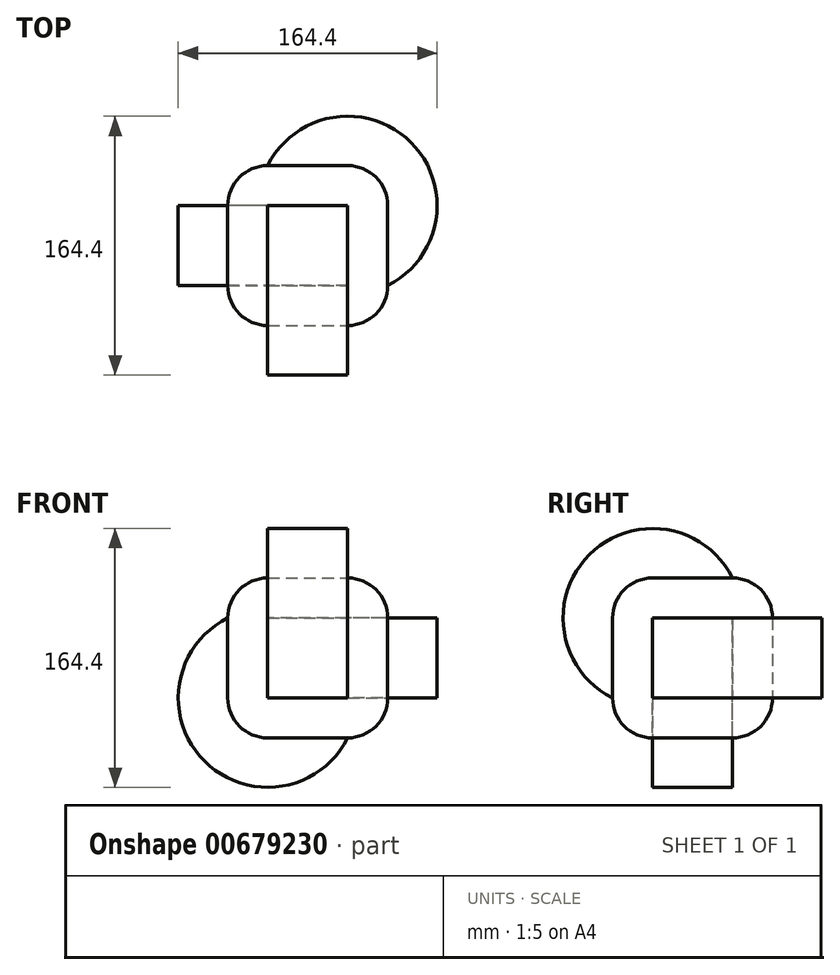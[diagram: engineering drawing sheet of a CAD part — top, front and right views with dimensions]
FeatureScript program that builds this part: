
annotation { "Feature Type Name" : "Feature", "Feature Type Description" : "" }
export const myFeature = defineFeature(function(context is Context, id is Id, definition is map)
    precondition{}
    {
        {
            var Q0;
            Q0=qCreatedBy(makeId("Top.planeOp"),FACE);
            var sketch = newSketch(context, id + "F0", { "sketchPlane" : qUnion([Q0])});
            skLineSegment(sketch, "E0.bottom", {"start": v(-50.8, 50.8) * mm, "end": v(50.8, 50.8) * mm});
            skLineSegment(sketch, "E0.top", {"start": v(-50.8, -50.8) * mm, "end": v(50.8, -50.8) * mm});
            skLineSegment(sketch, "E0.left", {"start": v(-50.8, 50.8) * mm, "end": v(-50.8, -50.8) * mm});
            skLineSegment(sketch, "E0.right", {"start": v(50.8, 50.8) * mm, "end": v(50.8, -50.8) * mm});
            skPoint(sketch, "E0.middle", {"position": v(0, 0) * mm});
            skSolve(sketch);
        }
        {
            var Q0;
            Q0 = qSketchRegion(id + "F0", true);
            extrude(context, id + "F1", {"entities" : qUnion([Q0]), "depth" : 101.6 * mm, "offsetDistance" : 25.4 * mm});
        }
        {
            var Q0;
            Q0=makeQuery(id+"F1.opExtrude","CAP_EDGE",EDGE,{"disambiguationData":[OSD([sQuery(id+"F0.wireOp",EDGE,"E0.right")])],"isStart":false});
            var Q1;
            Q1=makeQuery(id+"F1.opExtrude","CAP_EDGE",EDGE,{"disambiguationData":[OSD([sQuery(id+"F0.wireOp",EDGE,"E0.top")])],"isStart":false});
            var Q2;
            Q2=makeQuery(id+"F1.opExtrude","CAP_EDGE",EDGE,{"disambiguationData":[OSD([sQuery(id+"F0.wireOp",EDGE,"E0.left")])],"isStart":false});
            var Q3;
            Q3=makeQuery(id+"F1.opExtrude","CAP_EDGE",EDGE,{"disambiguationData":[OSD([sQuery(id+"F0.wireOp",EDGE,"E0.bottom")])],"isStart":false});
            var Q4;
            Q4=makeQuery(id+"F1.opExtrude","SWEPT_EDGE",EDGE,{"disambiguationData":[OSD([sQuery(id+"F0.wireOp",EDGE,"E0.bottom"),sQuery(id+"F0.wireOp",EDGE,"E0.right")])]});
            var Q5;
            Q5=makeQuery(id+"F1.opExtrude","SWEPT_EDGE",EDGE,{"disambiguationData":[OSD([sQuery(id+"F0.wireOp",EDGE,"E0.top"),sQuery(id+"F0.wireOp",EDGE,"E0.right")])]});
            var Q6;
            Q6=makeQuery(id+"F1.opExtrude","SWEPT_EDGE",EDGE,{"disambiguationData":[OSD([sQuery(id+"F0.wireOp",EDGE,"E0.top"),sQuery(id+"F0.wireOp",EDGE,"E0.left")])]});
            var Q7;
            Q7=makeQuery(id+"F1.opExtrude","CAP_EDGE",EDGE,{"disambiguationData":[OSD([sQuery(id+"F0.wireOp",EDGE,"E0.top")])],"isStart":true});
            var Q8;
            Q8=makeQuery(id+"F1.opExtrude","CAP_EDGE",EDGE,{"disambiguationData":[OSD([sQuery(id+"F0.wireOp",EDGE,"E0.right")])],"isStart":true});
            var Q9;
            Q9=makeQuery(id+"F1.opExtrude","CAP_EDGE",EDGE,{"disambiguationData":[OSD([sQuery(id+"F0.wireOp",EDGE,"E0.bottom")])],"isStart":true});
            var Q10;
            Q10=makeQuery(id+"F1.opExtrude","SWEPT_EDGE",EDGE,{"disambiguationData":[OSD([sQuery(id+"F0.wireOp",EDGE,"E0.bottom"),sQuery(id+"F0.wireOp",EDGE,"E0.left")])]});
            var Q11;
            Q11=makeQuery(id+"F1.opExtrude","CAP_EDGE",EDGE,{"disambiguationData":[OSD([sQuery(id+"F0.wireOp",EDGE,"E0.left")])],"isStart":true});
            fillet(context, id + "F2", {"entities" : qUnion([Q0, Q1, Q2, Q3, Q4, Q5, Q6, Q7, Q8, Q9, Q10, Q11]), "radius" : 25.4 * mm, "tangentPropagation" : true, "allowEdgeOverflow" : false});
        }
        {
            var Q0;
            Q0=makeQuery(id+"F1.opExtrude","CAP_FACE",FACE,{"disambiguationData":[OSD([sQuery(id+"F0.wireOp",EDGE,"E0.bottom"),sQuery(id+"F0.wireOp",EDGE,"E0.top"),sQuery(id+"F0.wireOp",EDGE,"E0.left"),sQuery(id+"F0.wireOp",EDGE,"E0.right")])],"isStart":false});
            var Q1;
            {var subQ0=sQuery(id+"F0.wireOp",EDGE,"E0.top");Q1=makeQuery(id+"F2.opFillet","BLEND_FACE",FACE,{"disambiguationData":[OSD([subQ0]),TDD([makeQuery(id+"F1.opExtrude","CAP_EDGE",EDGE,{"disambiguationData":[OSD([subQ0])],"isStart":false})])]});}
            revolve(context, id + "F3", {"operationType" : NewBodyOperationType.ADD, "surfaceOperationType" : NewSurfaceOperationType.NEW, "entities" : qUnion([Q0]), "axis" : qUnion([Q1]), "revolveType" : RevolveType.FULL});
        }
        {
            var Q0;
            Q0=makeQuery(id+"F1.opExtrude","SWEPT_FACE",FACE,{"disambiguationData":[OSD([sQuery(id+"F0.wireOp",EDGE,"E0.bottom")])]});
            var Q1;
            {var subQ0=sQuery(id+"F0.wireOp",EDGE,"E0.right");var subQ1=sQuery(id+"F0.wireOp",EDGE,"E0.bottom");Q1=makeQuery(id+"F2.opFillet","BLEND_FACE",FACE,{"disambiguationData":[OSD([subQ1,subQ0]),TDD([makeQuery(id+"F1.opExtrude","SWEPT_EDGE",EDGE,{"disambiguationData":[OSD([subQ1,subQ0])]})])]});}
            revolve(context, id + "F4", {"operationType" : NewBodyOperationType.ADD, "surfaceOperationType" : NewSurfaceOperationType.NEW, "entities" : qUnion([Q0]), "axis" : qUnion([Q1]), "revolveType" : RevolveType.FULL});
        }
        {
            var Q0;
            Q0=makeQuery(id+"F1.opExtrude","SWEPT_FACE",FACE,{"disambiguationData":[OSD([sQuery(id+"F0.wireOp",EDGE,"E0.left")])]});
            var Q1;
            {var subQ0=sQuery(id+"F0.wireOp",EDGE,"E0.left");Q1=makeQuery(id+"F2.opFillet","BLEND_FACE",FACE,{"disambiguationData":[OSD([subQ0]),TDD([makeQuery(id+"F1.opExtrude","CAP_EDGE",EDGE,{"disambiguationData":[OSD([subQ0])],"isStart":true})])]});}
            revolve(context, id + "F5", {"operationType" : NewBodyOperationType.ADD, "surfaceOperationType" : NewSurfaceOperationType.NEW, "entities" : qUnion([Q0]), "axis" : qUnion([Q1]), "revolveType" : RevolveType.FULL});
        }
    });
